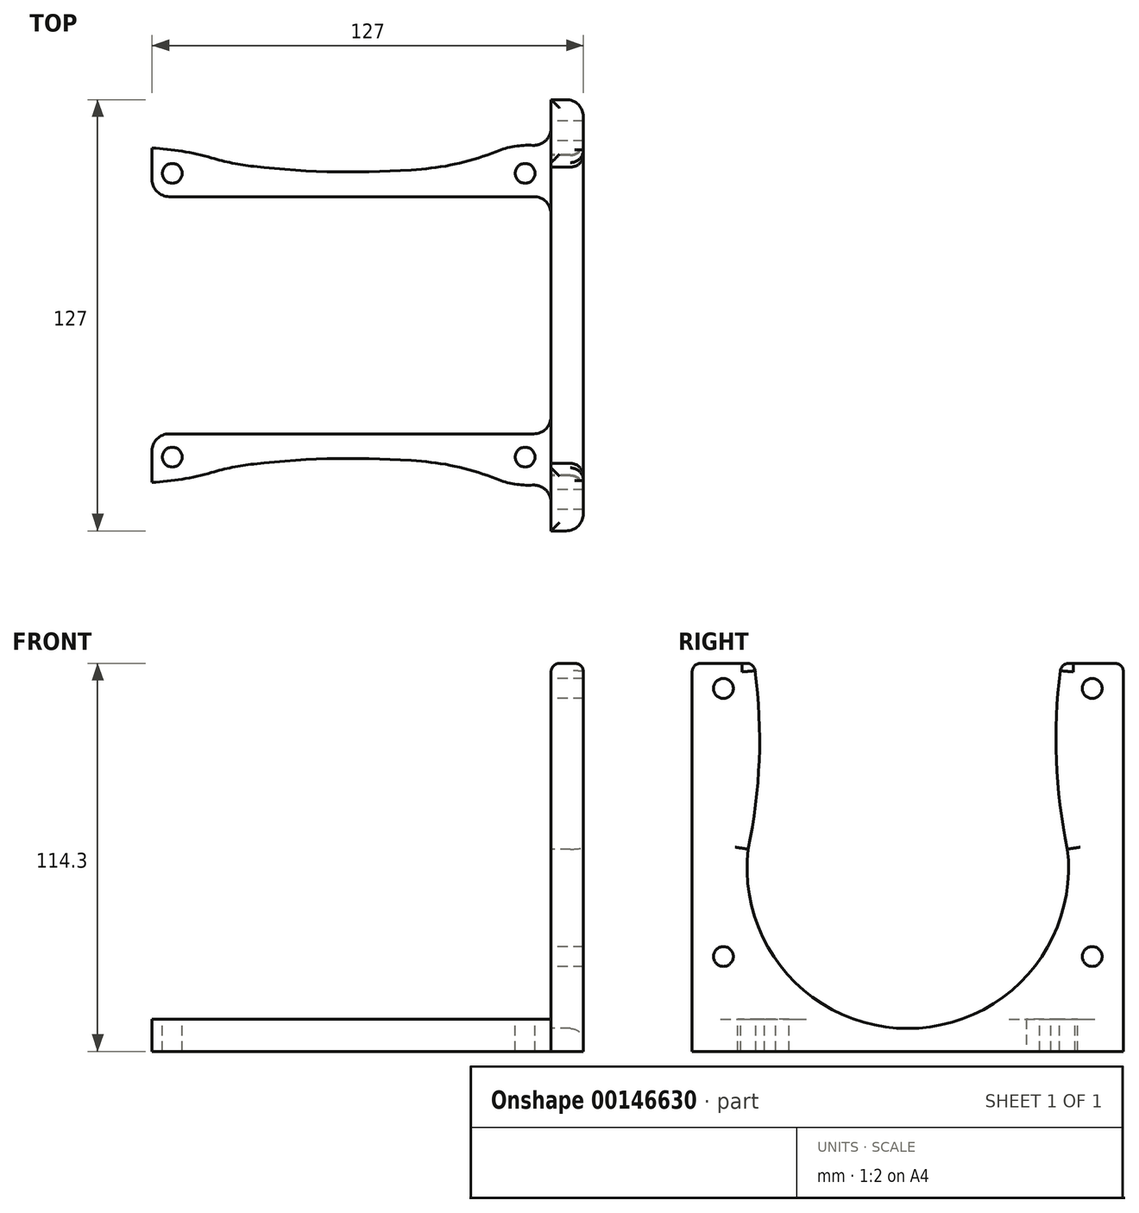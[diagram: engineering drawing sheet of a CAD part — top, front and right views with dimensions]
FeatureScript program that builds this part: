
annotation { "Feature Type Name" : "Feature", "Feature Type Description" : "" }
export const myFeature = defineFeature(function(context is Context, id is Id, definition is map)
    precondition{}
    {
        {
            var Q0;
            Q0=qCreatedBy(makeId("Front.planeOp"),FACE);
            var sketch = newSketch(context, id + "F0", { "sketchPlane" : qUnion([Q0])});
            skLineSegment(sketch, "E0.bottom", {"start": v(0, 0) * mm, "end": v(117.47, 0) * mm});
            skLineSegment(sketch, "E0.top", {"start": v(0, 9.52) * mm, "end": v(117.48, 9.53) * mm});
            skLineSegment(sketch, "E0.left", {"start": v(0, 0) * mm, "end": v(0, 9.52) * mm});
            skLineSegment(sketch, "E1.bottom", {"start": v(117.47, 0) * mm, "end": v(127, 0) * mm});
            skLineSegment(sketch, "E1.top", {"start": v(117.47, 114.3) * mm, "end": v(127, 114.3) * mm});
            skLineSegment(sketch, "E1.left", {"start": v(117.47, 9.53) * mm, "end": v(117.47, 114.3) * mm});
            skLineSegment(sketch, "E1.right", {"start": v(127, 0) * mm, "end": v(127, 114.3) * mm});
            skSolve(sketch);
        }
        {
            var Q0;
            Q0 = qSketchRegion(id + "F0", true);
            extrude(context, id + "F1", {"entities" : qUnion([Q0]), "endBound" : BoundingType.SYMMETRIC, "depth" : 127 * mm});
        }
        {
            var Q0;
            Q0=makeQuery(id+"F1.opExtrude","SWEPT_FACE",FACE,{"disambiguationData":[OSD([sQuery(id+"F0.wireOp",EDGE,"E1.left")])]});
            var sketch = newSketch(context, id + "F2", { "sketchPlane" : qUnion([Q0])});
            skCircle(sketch, "E2", {"center": v(-54.3, 106.88) * mm, "radius": 2.92 * mm});
            skCircle(sketch, "E3", {"center": v(54.3, 106.88) * mm, "radius": 2.92 * mm});
            skCircle(sketch, "E4", {"center": v(54.3, 27.94) * mm, "radius": 2.92 * mm});
            skCircle(sketch, "E5", {"center": v(-54.3, 27.94) * mm, "radius": 2.92 * mm});
            skLineSegment(sketch, "E6", {"start": v(-54.3, 106.88) * mm, "end": v(-54.3, 27.94) * mm, "construction": true});
            skLineSegment(sketch, "E7", {"start": v(-54.3, 27.94) * mm, "end": v(54.3, 27.94) * mm, "construction": true});
            skLineSegment(sketch, "E8", {"start": v(54.3, 27.94) * mm, "end": v(54.3, 106.88) * mm, "construction": true});
            skLineSegment(sketch, "E9", {"start": v(54.3, 106.88) * mm, "end": v(-54.3, 106.88) * mm, "construction": true});
            skLineSegment(sketch, "E10", {"start": v(0, 114.3) * mm, "end": v(0, 106.88) * mm, "construction": true});
            skSolve(sketch);
        }
        {
            var Q0;
            Q0 = qSketchRegion(id + "F2", true);
            extrude(context, id + "F3", {"entities" : qUnion([Q0]), "operationType" : NewBodyOperationType.REMOVE, "oppositeDirection" : true, "depth" : 25.4 * mm});
        }
        {
            var Q0;
            Q0=makeQuery(id+"F1.opExtrude","SWEPT_FACE",FACE,{"disambiguationData":[OSD([sQuery(id+"F0.wireOp",EDGE,"E0.top")])]});
            var sketch = newSketch(context, id + "F4", { "sketchPlane" : qUnion([Q0])});
            skCircle(sketch, "E11", {"center": v(5.97, 41.78) * mm, "radius": 2.92 * mm});
            skCircle(sketch, "E12", {"center": v(5.97, -41.78) * mm, "radius": 2.92 * mm});
            skCircle(sketch, "E13", {"center": v(109.85, -41.78) * mm, "radius": 2.92 * mm});
            skCircle(sketch, "E14", {"center": v(109.85, 41.78) * mm, "radius": 2.92 * mm});
            skLineSegment(sketch, "E15", {"start": v(5.97, 41.78) * mm, "end": v(109.85, 41.78) * mm, "construction": true});
            skLineSegment(sketch, "E16", {"start": v(109.85, 41.78) * mm, "end": v(109.85, -41.78) * mm, "construction": true});
            skLineSegment(sketch, "E17", {"start": v(109.85, -41.78) * mm, "end": v(5.97, -41.78) * mm, "construction": true});
            skLineSegment(sketch, "E18", {"start": v(5.97, -41.78) * mm, "end": v(5.97, 41.78) * mm, "construction": true});
            skLineSegment(sketch, "E19", {"start": v(0, 0) * mm, "end": v(5.97, 0) * mm, "construction": true});
            skSolve(sketch);
        }
        {
            var Q0;
            Q0 = qSketchRegion(id + "F4", true);
            extrude(context, id + "F5", {"entities" : qUnion([Q0]), "operationType" : NewBodyOperationType.REMOVE, "oppositeDirection" : true, "depth" : 25.4 * mm});
        }
        {
            var Q0;
            Q0=qCreatedBy(makeId("Front.planeOp"),FACE);
            var sketch = newSketch(context, id + "F6", { "sketchPlane" : qUnion([Q0])});
            skLineSegment(sketch, "E20", {"start": v(91.08, 0) * mm, "end": v(127, 35.92) * mm});
            skLineSegment(sketch, "E21", {"start": v(127, 35.92) * mm, "end": v(127, 0) * mm});
            skLineSegment(sketch, "E22", {"start": v(127, 0) * mm, "end": v(91.08, 0) * mm});
            skSolve(sketch);
        }
        {
            var Q0;
            Q0=makeQuery(id+"F1.opExtrude","CAP_FACE",FACE,{"disambiguationData":[OSD([sQuery(id+"F0.wireOp",EDGE,"E0.bottom"),sQuery(id+"F0.wireOp",EDGE,"E0.top"),sQuery(id+"F0.wireOp",EDGE,"E0.left"),sQuery(id+"F0.wireOp",EDGE,"E1.bottom"),sQuery(id+"F0.wireOp",EDGE,"E1.top"),sQuery(id+"F0.wireOp",EDGE,"E1.left"),sQuery(id+"F0.wireOp",EDGE,"E1.right")])],"isStart":false});
            var sketch = newSketch(context, id + "F7", { "sketchPlane" : qUnion([Q0])});
            skLineSegment(sketch, "E23", {"start": v(91.08, 0) * mm, "end": v(127, 35.92) * mm});
            skLineSegment(sketch, "E24", {"start": v(127, 35.92) * mm, "end": v(127, 0) * mm});
            skLineSegment(sketch, "E25", {"start": v(127, 0) * mm, "end": v(91.08, 0) * mm});
            skSolve(sketch);
        }
        {
            var Q0;
            Q0=makeQuery(id+"F1.opExtrude","CAP_FACE",FACE,{"disambiguationData":[OSD([sQuery(id+"F0.wireOp",EDGE,"E0.bottom"),sQuery(id+"F0.wireOp",EDGE,"E0.top"),sQuery(id+"F0.wireOp",EDGE,"E0.left"),sQuery(id+"F0.wireOp",EDGE,"E1.bottom"),sQuery(id+"F0.wireOp",EDGE,"E1.top"),sQuery(id+"F0.wireOp",EDGE,"E1.left"),sQuery(id+"F0.wireOp",EDGE,"E1.right")])],"isStart":true});
            var sketch = newSketch(context, id + "F8", { "sketchPlane" : qUnion([Q0])});
            skLineSegment(sketch, "E26", {"start": v(-127, 0) * mm, "end": v(-91.08, 0) * mm});
            skLineSegment(sketch, "E27", {"start": v(-91.08, 0) * mm, "end": v(-127, 35.92) * mm});
            skLineSegment(sketch, "E28", {"start": v(-127, 35.92) * mm, "end": v(-127, 0) * mm});
            skSolve(sketch);
        }
        {
            var Q0;
            Q0=makeQuery(id+"F1.opExtrude","SWEPT_FACE",FACE,{"disambiguationData":[OSD([sQuery(id+"F0.wireOp",EDGE,"E1.left")])]});
            var sketch = newSketch(context, id + "F9", { "sketchPlane" : qUnion([Q0])});
            skLineSegment(sketch, "E29.bottom", {"start": v(34.93, 51.94) * mm, "end": v(-34.93, 51.94) * mm});
            skLineSegment(sketch, "E29.top", {"start": v(34.93, -51.94) * mm, "end": v(-34.93, -51.94) * mm});
            skLineSegment(sketch, "E29.left", {"start": v(34.93, 51.94) * mm, "end": v(34.93, -51.94) * mm});
            skLineSegment(sketch, "E29.right", {"start": v(-34.93, 51.94) * mm, "end": v(-34.93, -51.94) * mm});
            skPoint(sketch, "E29.middle", {"position": v(0, 0) * mm});
            skSolve(sketch);
        }
        {
            var Q0;
            Q0 = qSketchRegion(id + "F9", true);
            extrude(context, id + "F10", {"entities" : qUnion([Q0]), "operationType" : NewBodyOperationType.REMOVE, "depth" : 125.1 * mm});
        }
        {
            var Q0;
            {var subQ2=sQuery(id+"F0.wireOp",EDGE,"E0.top");Q0=makeQuery(id+"F10.boolean.opBoolean","SPLIT",FACE,{"disambiguationData":[TD([makeQuery(id+"F5.boolean.opBoolean","COPY",FACE,{"derivedFrom":makeQuery(id+"F5.opExtrude","SWEPT_FACE",FACE,{"disambiguationData":[OSD([sQuery(id+"F4.wireOp",EDGE,"E11")])]})})])],"derivedFrom":makeQuery(id+"F1.opExtrude","SWEPT_FACE",FACE,{"disambiguationData":[OSD([subQ2])]})});}
            var sketch = newSketch(context, id + "F11", { "sketchPlane" : qUnion([Q0])});
            skArc(sketch, "E30", {"start": v(21.99, 44.88) * mm, "mid": v(11.15, 47.86) * mm, "end": v(0, 49.21) * mm});
            skArc(sketch, "E31", {"start": v(21.99, 44.88) * mm, "mid": v(58.74, 42.18) * mm, "end": v(95.49, 44.88) * mm});
            skArc(sketch, "E32", {"start": v(117.47, 49.21) * mm, "mid": v(105.98, 49.58) * mm, "end": v(95.49, 44.88) * mm});
            skLineSegment(sketch, "E33", {"start": v(0, 49.21) * mm, "end": v(0, 63.5) * mm});
            skLineSegment(sketch, "E34", {"start": v(0, 63.5) * mm, "end": v(117.47, 63.5) * mm});
            skLineSegment(sketch, "E35", {"start": v(117.47, 63.5) * mm, "end": v(117.47, 49.21) * mm});
            skLineSegment(sketch, "E36", {"start": v(58.74, 293.87) * mm, "end": v(58.74, -34.93) * mm, "construction": true});
            skLineSegment(sketch, "E37", {"start": v(21.99, 44.88) * mm, "end": v(95.49, 44.88) * mm, "construction": true});
            skArc(sketch, "E38.MirrorCS", {"start": v(21.99, -44.88) * mm, "mid": v(58.74, -42.18) * mm, "end": v(95.49, -44.88) * mm});
            skArc(sketch, "E39.MirrorCS", {"start": v(21.99, -44.88) * mm, "mid": v(11.15, -47.86) * mm, "end": v(0, -49.21) * mm});
            skLineSegment(sketch, "E40.MirrorCS", {"start": v(0, -49.21) * mm, "end": v(0, -63.5) * mm});
            skLineSegment(sketch, "E41.MirrorCS", {"start": v(0, -63.5) * mm, "end": v(117.47, -63.5) * mm});
            skLineSegment(sketch, "E42.MirrorCS", {"start": v(117.47, -63.5) * mm, "end": v(117.47, -49.21) * mm});
            skArc(sketch, "E43.MirrorCS", {"start": v(117.47, -49.21) * mm, "mid": v(105.98, -49.58) * mm, "end": v(95.49, -44.88) * mm});
            skSolve(sketch);
        }
        {
            var Q0;
            Q0 = qSketchRegion(id + "F11", true);
            extrude(context, id + "F12", {"entities" : qUnion([Q0]), "operationType" : NewBodyOperationType.REMOVE, "oppositeDirection" : true, "depth" : 25.4 * mm});
        }
        {
            var Q0;
            Q0=makeQuery(id+"F12.boolean.opBoolean","COPY",EDGE,{"derivedFrom":makeQuery(id+"F12.opExtrude","SWEPT_EDGE",EDGE,{"disambiguationData":[OSD([sQuery(id+"F0.wireOp",EDGE,"E0.top"),sQuery(id+"F0.wireOp",EDGE,"E1.left"),sQuery(id+"F11.wireOp",EDGE,"E32"),sQuery(id+"F11.wireOp",EDGE,"E35")])]})});
            var Q1;
            Q1=makeQuery(id+"F12.boolean.opBoolean","COPY",EDGE,{"derivedFrom":makeQuery(id+"F12.opExtrude","SWEPT_EDGE",EDGE,{"disambiguationData":[OSD([sQuery(id+"F0.wireOp",EDGE,"E0.top"),sQuery(id+"F0.wireOp",EDGE,"E0.left"),sQuery(id+"F11.wireOp",EDGE,"E30"),sQuery(id+"F11.wireOp",EDGE,"E33")])]})});
            var Q2;
            Q2=makeQuery(id+"F10.boolean.opBoolean","INTERSECT",EDGE,{"derivedFrom":[makeQuery(id+"F1.opExtrude","SWEPT_FACE",FACE,{"disambiguationData":[OSD([sQuery(id+"F0.wireOp",EDGE,"E0.left")])]}),makeQuery(id+"F10.opExtrude","SWEPT_FACE",FACE,{"disambiguationData":[OSD([sQuery(id+"F9.wireOp",EDGE,"E29.right")])]})]});
            var Q3;
            Q3=makeQuery(id+"F10.boolean.opBoolean","COPY",EDGE,{"derivedFrom":makeQuery(id+"F10.opExtrude","CAP_EDGE",EDGE,{"disambiguationData":[OSD([sQuery(id+"F9.wireOp",EDGE,"E29.right")])],"isStart":true})});
            var Q4;
            Q4=makeQuery(id+"F10.boolean.opBoolean","COPY",EDGE,{"derivedFrom":makeQuery(id+"F10.opExtrude","CAP_EDGE",EDGE,{"disambiguationData":[OSD([sQuery(id+"F9.wireOp",EDGE,"E29.left")])],"isStart":true})});
            var Q5;
            Q5=makeQuery(id+"F10.boolean.opBoolean","INTERSECT",EDGE,{"derivedFrom":[makeQuery(id+"F1.opExtrude","SWEPT_FACE",FACE,{"disambiguationData":[OSD([sQuery(id+"F0.wireOp",EDGE,"E0.left")])]}),makeQuery(id+"F10.opExtrude","SWEPT_FACE",FACE,{"disambiguationData":[OSD([sQuery(id+"F9.wireOp",EDGE,"E29.left")])]})]});
            var Q6;
            Q6=makeQuery(id+"F12.boolean.opBoolean","COPY",EDGE,{"derivedFrom":makeQuery(id+"F12.opExtrude","SWEPT_EDGE",EDGE,{"disambiguationData":[OSD([sQuery(id+"F11.wireOp",EDGE,"E39.MirrorCS"),sQuery(id+"F11.wireOp",EDGE,"E40.MirrorCS")])]})});
            var Q7;
            Q7=makeQuery(id+"F12.boolean.opBoolean","COPY",EDGE,{"derivedFrom":makeQuery(id+"F12.opExtrude","SWEPT_EDGE",EDGE,{"disambiguationData":[OSD([sQuery(id+"F11.wireOp",EDGE,"E42.MirrorCS"),sQuery(id+"F11.wireOp",EDGE,"E43.MirrorCS")])]})});
            fillet(context, id + "F13", {"entities" : qUnion([Q0, Q1, Q2, Q3, Q4, Q5, Q6, Q7]), "radius" : 5.08 * mm, "tangentPropagation" : true, "allowEdgeOverflow" : false});
        }
        {
            var Q0;
            Q0=makeQuery(id+"F12.boolean.opBoolean","COPY",EDGE,{"derivedFrom":makeQuery(id+"F12.opExtrude","SWEPT_EDGE",EDGE,{"disambiguationData":[OSD([sQuery(id+"F11.wireOp",EDGE,"E30"),sQuery(id+"F11.wireOp",EDGE,"E31")])]})});
            var Q1;
            Q1=makeQuery(id+"F12.boolean.opBoolean","COPY",EDGE,{"derivedFrom":makeQuery(id+"F12.opExtrude","SWEPT_EDGE",EDGE,{"disambiguationData":[OSD([sQuery(id+"F11.wireOp",EDGE,"E31"),sQuery(id+"F11.wireOp",EDGE,"E32")])]})});
            var Q2;
            Q2=makeQuery(id+"F12.boolean.opBoolean","COPY",EDGE,{"derivedFrom":makeQuery(id+"F12.opExtrude","SWEPT_EDGE",EDGE,{"disambiguationData":[OSD([sQuery(id+"F11.wireOp",EDGE,"E38.MirrorCS"),sQuery(id+"F11.wireOp",EDGE,"E39.MirrorCS")])]})});
            var Q3;
            Q3=makeQuery(id+"F12.boolean.opBoolean","COPY",EDGE,{"derivedFrom":makeQuery(id+"F12.opExtrude","SWEPT_EDGE",EDGE,{"disambiguationData":[OSD([sQuery(id+"F11.wireOp",EDGE,"E38.MirrorCS"),sQuery(id+"F11.wireOp",EDGE,"E43.MirrorCS")])]})});
            fillet(context, id + "F14", {"entities" : qUnion([Q0, Q1, Q2, Q3]), "radius" : 76.2 * mm, "tangentPropagation" : true, "allowEdgeOverflow" : false});
        }
        {
            var Q0;
            Q0=makeQuery(id+"F12.boolean.opBoolean","MERGE",FACE,{"derivedFrom":[makeQuery(id+"F10.boolean.opBoolean","MERGE",FACE,{"derivedFrom":[makeQuery(id+"F1.opExtrude","SWEPT_FACE",FACE,{"disambiguationData":[OSD([sQuery(id+"F0.wireOp",EDGE,"E1.left")])]}),makeQuery(id+"F10.opExtrude","CAP_FACE",FACE,{"disambiguationData":[OSD([sQuery(id+"F9.wireOp",EDGE,"E29.bottom"),sQuery(id+"F9.wireOp",EDGE,"E29.top"),sQuery(id+"F9.wireOp",EDGE,"E29.left"),sQuery(id+"F9.wireOp",EDGE,"E29.right")])],"isStart":true})]}),makeQuery(id+"F12.opExtrude","SWEPT_FACE",FACE,{"disambiguationData":[OSD([sQuery(id+"F11.wireOp",EDGE,"E35")])]}),makeQuery(id+"F12.opExtrude","SWEPT_FACE",FACE,{"disambiguationData":[OSD([sQuery(id+"F11.wireOp",EDGE,"E42.MirrorCS")])]})]});
            var sketch = newSketch(context, id + "F15", { "sketchPlane" : qUnion([Q0])});
            skArc(sketch, "E44", {"start": v(-47.01, 59.54) * mm, "mid": v(0, 6.75) * mm, "end": v(47.01, 59.54) * mm});
            skArc(sketch, "E45", {"start": v(-47.01, 59.54) * mm, "mid": v(-43.7, 86.84) * mm, "end": v(-45.25, 114.3) * mm});
            skArc(sketch, "E46.MirrorCS", {"start": v(47.01, 59.54) * mm, "mid": v(43.7, 86.84) * mm, "end": v(45.25, 114.3) * mm});
            skLineSegment(sketch, "E47", {"start": v(-45.25, 114.3) * mm, "end": v(45.25, 114.3) * mm});
            skSolve(sketch);
        }
        {
            var Q0;
            Q0 = qSketchRegion(id + "F15", true);
            extrude(context, id + "F16", {"entities" : qUnion([Q0]), "operationType" : NewBodyOperationType.REMOVE, "oppositeDirection" : true, "depth" : 25.4 * mm});
        }
        {
            var Q0;
            Q0=makeQuery(id+"F16.boolean.opBoolean","COPY",EDGE,{"derivedFrom":makeQuery(id+"F16.opExtrude","CAP_EDGE",EDGE,{"disambiguationData":[OSD([sQuery(id+"F15.wireOp",EDGE,"E44")])],"isStart":true})});
            var Q1;
            Q1=makeQuery(id+"F16.boolean.opBoolean","COPY",EDGE,{"derivedFrom":makeQuery(id+"F16.opExtrude","CAP_EDGE",EDGE,{"disambiguationData":[OSD([sQuery(id+"F15.wireOp",EDGE,"E45")])],"isStart":true})});
            var Q2;
            Q2=makeQuery(id+"F16.boolean.opBoolean","COPY",EDGE,{"derivedFrom":makeQuery(id+"F16.opExtrude","CAP_EDGE",EDGE,{"disambiguationData":[OSD([sQuery(id+"F15.wireOp",EDGE,"E46.MirrorCS")])],"isStart":true})});
            var Q3;
            Q3=makeQuery(id+"F12.boolean.opBoolean","MERGE",EDGE,{"derivedFrom":[makeQuery(id+"F1.opExtrude","CAP_EDGE",EDGE,{"disambiguationData":[OSD([sQuery(id+"F0.wireOp",EDGE,"E1.left")])],"isStart":false}),makeQuery(id+"F12.opExtrude","SWEPT_EDGE",EDGE,{"disambiguationData":[OSD([sQuery(id+"F11.wireOp",EDGE,"E41.MirrorCS"),sQuery(id+"F11.wireOp",EDGE,"E42.MirrorCS")])]})]});
            var Q4;
            Q4=makeQuery(id+"F12.boolean.opBoolean","MERGE",EDGE,{"derivedFrom":[makeQuery(id+"F1.opExtrude","CAP_EDGE",EDGE,{"disambiguationData":[OSD([sQuery(id+"F0.wireOp",EDGE,"E1.left")])],"isStart":true}),makeQuery(id+"F12.opExtrude","SWEPT_EDGE",EDGE,{"disambiguationData":[OSD([sQuery(id+"F11.wireOp",EDGE,"E34"),sQuery(id+"F11.wireOp",EDGE,"E35")])]})]});
            var Q5;
            Q5=makeQuery(id+"F1.opExtrude","CAP_EDGE",EDGE,{"disambiguationData":[OSD([sQuery(id+"F0.wireOp",EDGE,"E1.right")])],"isStart":true});
            var Q6;
            Q6=makeQuery(id+"F1.opExtrude","CAP_EDGE",EDGE,{"disambiguationData":[OSD([sQuery(id+"F0.wireOp",EDGE,"E1.right")])],"isStart":false});
            fillet(context, id + "F17", {"entities" : qUnion([Q0, Q1, Q2, Q3, Q4, Q5, Q6]), "radius" : 5.08 * mm, "tangentPropagation" : true, "allowEdgeOverflow" : false});
        }
        {
            var Q0;
            Q0=makeQuery(id+"F16.boolean.opBoolean","INTERSECT",EDGE,{"derivedFrom":[makeQuery(id+"F1.opExtrude","SWEPT_FACE",FACE,{"disambiguationData":[OSD([sQuery(id+"F0.wireOp",EDGE,"E1.right")])]}),makeQuery(id+"F16.opExtrude","SWEPT_FACE",FACE,{"disambiguationData":[OSD([sQuery(id+"F15.wireOp",EDGE,"E45")])]})]});
            var Q1;
            Q1=makeQuery(id+"F16.boolean.opBoolean","INTERSECT",EDGE,{"derivedFrom":[makeQuery(id+"F1.opExtrude","SWEPT_FACE",FACE,{"disambiguationData":[OSD([sQuery(id+"F0.wireOp",EDGE,"E1.right")])]}),makeQuery(id+"F16.opExtrude","SWEPT_FACE",FACE,{"disambiguationData":[OSD([sQuery(id+"F15.wireOp",EDGE,"E44")])]})]});
            var Q2;
            Q2=makeQuery(id+"F16.boolean.opBoolean","INTERSECT",EDGE,{"derivedFrom":[makeQuery(id+"F1.opExtrude","SWEPT_FACE",FACE,{"disambiguationData":[OSD([sQuery(id+"F0.wireOp",EDGE,"E1.right")])]}),makeQuery(id+"F16.opExtrude","SWEPT_FACE",FACE,{"disambiguationData":[OSD([sQuery(id+"F15.wireOp",EDGE,"E46.MirrorCS")])]})]});
            fillet(context, id + "F18", {"entities" : qUnion([Q0, Q1, Q2]), "radius" : 3.8 * mm, "tangentPropagation" : true, "allowEdgeOverflow" : false});
        }
        {
            var Q0;
            {var subQ2=sQuery(id+"F0.wireOp",EDGE,"E1.top");Q0=makeQuery(id+"F16.boolean.opBoolean","SPLIT",FACE,{"disambiguationData":[TD([makeQuery(id+"F16.opExtrude","SWEPT_FACE",FACE,{"disambiguationData":[OSD([sQuery(id+"F15.wireOp",EDGE,"E45")])]})])],"derivedFrom":makeQuery(id+"F1.opExtrude","SWEPT_FACE",FACE,{"disambiguationData":[OSD([subQ2])]})});}
            var Q1;
            {var subQ2=sQuery(id+"F0.wireOp",EDGE,"E1.top");Q1=makeQuery(id+"F16.boolean.opBoolean","SPLIT",FACE,{"disambiguationData":[TD([makeQuery(id+"F16.opExtrude","SWEPT_FACE",FACE,{"disambiguationData":[OSD([sQuery(id+"F15.wireOp",EDGE,"E46.MirrorCS")])]})])],"derivedFrom":makeQuery(id+"F1.opExtrude","SWEPT_FACE",FACE,{"disambiguationData":[OSD([subQ2])]})});}
            fillet(context, id + "F19", {"entities" : qUnion([Q0, Q1]), "radius" : 2.54 * mm, "tangentPropagation" : true, "allowEdgeOverflow" : false});
        }
    });
